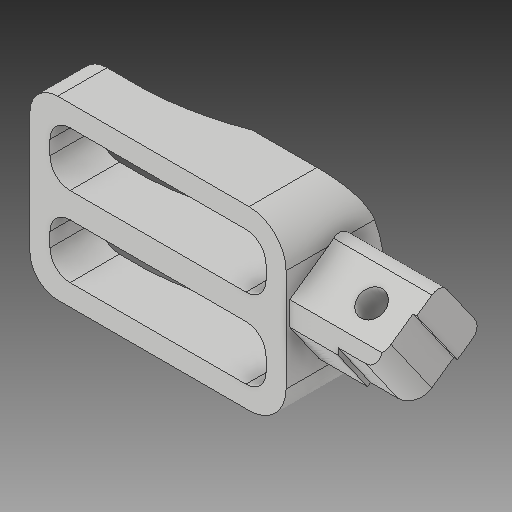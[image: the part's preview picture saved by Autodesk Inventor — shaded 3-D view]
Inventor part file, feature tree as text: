
AUTODESK INVENTOR PART (.ipt)
format: ipt  version: 2019.2 (Build 232265000, 265)  size: 293,376 bytes
history: native  units: mm
features: sketch x8, extrude x7, hole x1
ambient origin geometry x8: Origin, YZ Plane, XZ Plane, XY Plane, X Axis, Y Axis, Z Axis, Center Point
bodies: Solid1 (feature_tree)
feature tree (16):
  extrude  "Extrusion1"  Depth=57.2mm
  extrude  "Extrusion2"  Depth=12.0mm
  extrude  "Extrusion3"  Depth=17.6mm
  extrude  "Extrusion5"  Depth=6.5mm
  extrude  "Extrusion6"  Depth=22.0mm
  extrude  "Extrusion7"  Depth=31.75mm TaperAngle=0.0deg
  hole  "Hole1"  [1 undecoded]
  extrude  "Extrusion8"  Depth=3.0mm
  sketch  "Sketch1"  dims[d0=83.0mm d1=57.2mm]
  sketch  "Sketch2"  dims[d2=9.0mm d3=12.0mm]
  sketch  "Sketch3"  dims[d4=70.0mm d5=17.6mm]
  sketch  "Sketch4"  dims[d6=6.88mm d7=6.5mm]
  sketch  "Sketch5"  dims[d8=31.75mm d9=0.0mm d10=22.0mm]
  sketch  "Sketch6"  dims[d11=22.0mm d12=31.75mm d13=0.0mm]
  sketch  "Sketch7"  dims[d15=25.4mm d16=23.0mm]
  sketch  "Sketch8"  dims[d17=31.75mm d18=0.0mm d21=1.2mm d22=31.75mm d23=0.0mm d24=3.5mm d25=9.5mm d26=15.63mm d27=7.2mm d28=1.2mm d29=31.75mm d30=0.0mm d31=31.75mm d32=0.0mm d33=11.2mm d34=12.0mm d35=8.5mm d36=6.0mm d37=4.0mm d38=2.0mm d39=90.0deg d40=8.0mm d41=20.594885mm d42=9.599311mm d44=16.0mm d45=22.0mm d46=14.0mm d47=3.0mm d48=31.75mm d49=0.0mm]
note: 1 required parameter value undecoded (feature->parameter linkage not recoverable at this tier; creation-order binding heuristic only, values carry confidence <= 0.55)
